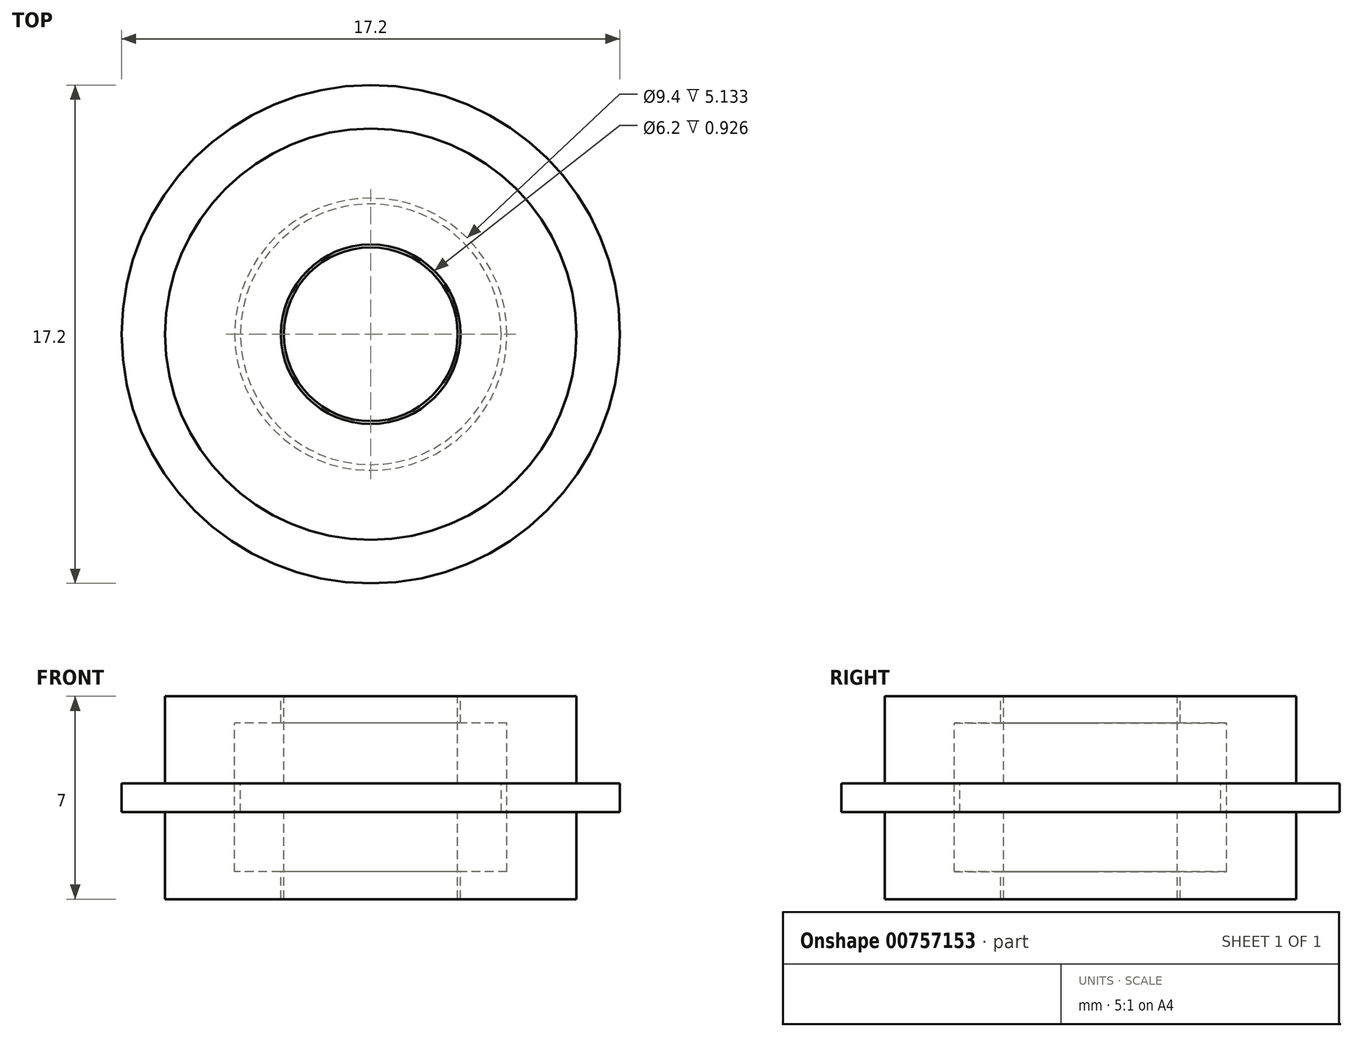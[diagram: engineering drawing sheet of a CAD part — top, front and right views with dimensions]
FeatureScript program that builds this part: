
annotation { "Feature Type Name" : "Feature", "Feature Type Description" : "" }
export const myFeature = defineFeature(function(context is Context, id is Id, definition is map)
    precondition{}
    {
        {
            var Q0;
            Q0=qCreatedBy(makeId("Front.planeOp"),FACE);
            var sketch = newSketch(context, id + "F0", { "sketchPlane" : qUnion([Q0])});
            skLineSegment(sketch, "E0", {"start": v(0, 0) * mm, "end": v(-3, 0) * mm});
            skLineSegment(sketch, "E1", {"start": v(-3, 0) * mm, "end": v(-3, 3) * mm});
            skLineSegment(sketch, "E2", {"start": v(-3, 3) * mm, "end": v(-4.5, 3) * mm});
            skLineSegment(sketch, "E3", {"start": v(-4.5, 3) * mm, "end": v(-4.5, 4) * mm});
            skLineSegment(sketch, "E4", {"start": v(-4.5, 4) * mm, "end": v(-3, 4) * mm});
            skLineSegment(sketch, "E5", {"start": v(-3, 4) * mm, "end": v(-3, 7) * mm});
            skLineSegment(sketch, "E6", {"start": v(-3, 7) * mm, "end": v(0, 7) * mm});
            skLineSegment(sketch, "E7", {"start": v(0, 7) * mm, "end": v(0, 0) * mm});
            skLineSegment(sketch, "E8", {"start": v(-3.1, 0) * mm, "end": v(-3.1, 0.94) * mm});
            skLineSegment(sketch, "E9", {"start": v(-3.1, 0.94) * mm, "end": v(-4.7, 0.94) * mm});
            skLineSegment(sketch, "E10", {"start": v(-4.7, 0.94) * mm, "end": v(-4.7, 6.07) * mm});
            skLineSegment(sketch, "E11", {"start": v(-4.7, 6.07) * mm, "end": v(-3.1, 6.07) * mm});
            skLineSegment(sketch, "E12", {"start": v(-3.1, 6.07) * mm, "end": v(-3.1, 7) * mm});
            skLineSegment(sketch, "E13", {"start": v(-3.1, 7) * mm, "end": v(-7.1, 7) * mm});
            skLineSegment(sketch, "E14", {"start": v(-7.1, 7) * mm, "end": v(-7.1, 4) * mm});
            skLineSegment(sketch, "E15", {"start": v(-7.1, 4) * mm, "end": v(-8.6, 4) * mm});
            skLineSegment(sketch, "E16", {"start": v(-8.6, 4) * mm, "end": v(-8.6, 3) * mm});
            skLineSegment(sketch, "E17", {"start": v(-8.6, 3) * mm, "end": v(-7.1, 3) * mm});
            skLineSegment(sketch, "E18", {"start": v(-7.1, 3) * mm, "end": v(-7.1, 0) * mm});
            skLineSegment(sketch, "E19", {"start": v(-7.1, 0) * mm, "end": v(-3.1, 0) * mm});
            skSolve(sketch);
        }
        {
            var Q0;
            Q0=makeQuery(id+"F0.imprint","IMPRINT",FACE,{"disambiguationData":[TD([[makeQuery(id+"F0.imprint","IMPRINT",EDGE,{"derivedFrom":sQuery(id+"F0.wireOp",EDGE,"E8")}),1.0]])]});
            var Q1;
            Q1=makeQuery(id+"F0.imprint","IMPRINT",FACE,{"disambiguationData":[TD([[makeQuery(id+"F0.imprint","IMPRINT",EDGE,{"derivedFrom":sQuery(id+"F0.wireOp",EDGE,"E0")}),-1.0]])]});
            var Q2;
            Q2=sQuery(id+"F0.wireOp",EDGE,"E7");
            revolve(context, id + "F1", {"surfaceOperationType" : NewSurfaceOperationType.NEW, "entities" : qUnion([Q0, Q1]), "axis" : qUnion([Q2]), "revolveType" : RevolveType.FULL});
        }
    });
